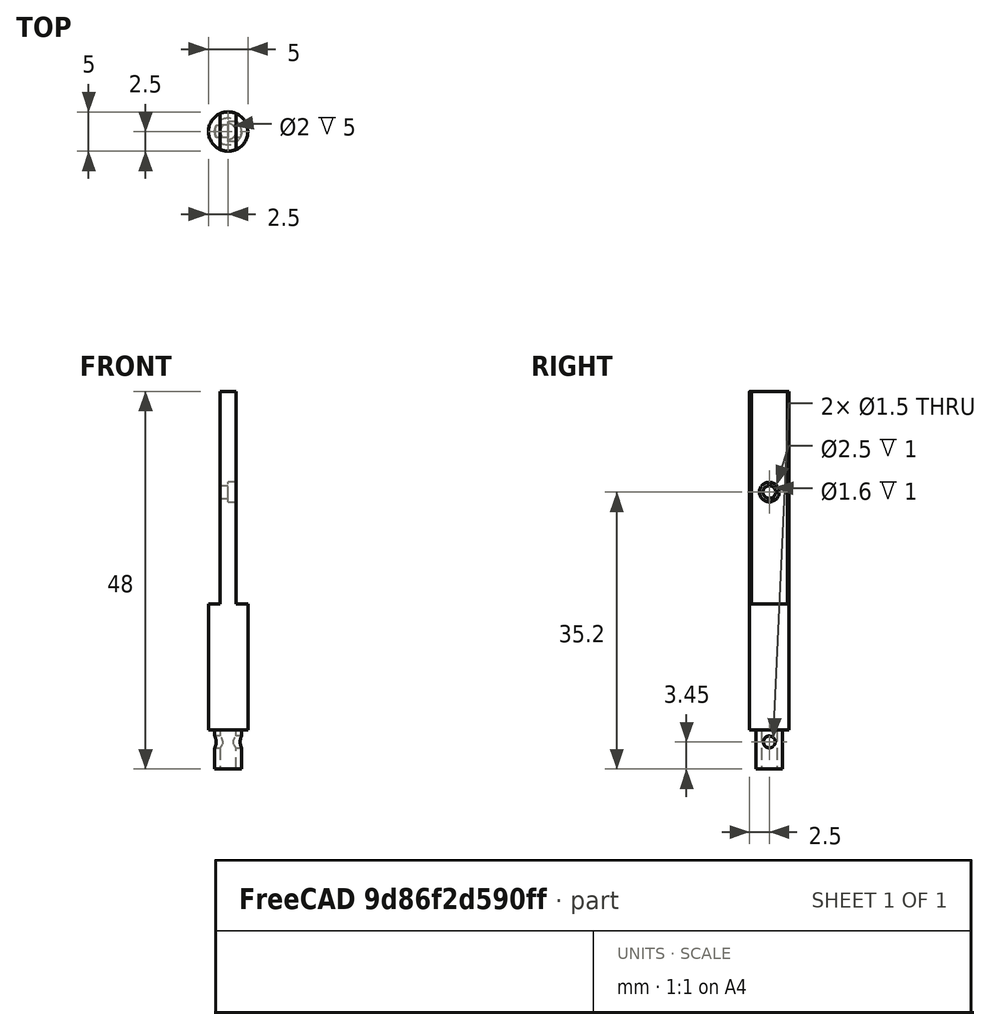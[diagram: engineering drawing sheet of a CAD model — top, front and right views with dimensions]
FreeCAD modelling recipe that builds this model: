
FCSTD DOCUMENT  (FreeCAD 0.20R29603 (Git))
Label: temholder
License: All rights reserved
LicenseURL: http://en.wikipedia.org/wiki/All_rights_reserved
objects: Part::Cylinder×7, Part::Cut×4, Part::MultiFuse×2, Part::Box×1, Part::MultiCommon×1, Part::Feature×1
note: 16 computed .brp shape members not serialized (recipe doc carries the construction recipe); baked Part::Feature solids carry a one-line shape summary decoded from their .brp

FEATURE [Part::Cylinder] Cylinder  label="Zylinder"
  Angle = 360
  AttacherType = Attacher::AttachEngine3D
  FirstAngle = 0
  Height = 21
  Radius = 1.7
  SecondAngle = 0
FEATURE [Part::Cylinder] Cylinder001  label="Zylinder001"
  Angle = 360
  AttacherType = Attacher::AttachEngine3D
  FirstAngle = 0
  Height = 16
  Placement = pos=(0,0,5) rot=(0,0,1;0rad)
  Radius = 2.5
  SecondAngle = 0
FEATURE [Part::Cylinder] Cylinder002  label="Zylinder002"
  Angle = 360
  AttacherType = Attacher::AttachEngine3D
  FirstAngle = 0
  Height = 6.5
  Placement = pos=(-3.25,0,3.45) rot=(0,1,0;1.5708rad)
  Radius = 0.75
  SecondAngle = 0
FEATURE [Part::MultiFuse] Fusion
  Shapes = -> [Cylinder,Cylinder001]
FEATURE [Part::Cut] Cut
  Base = -> Fusion
  Tool = -> Cylinder002
FEATURE [Part::Box] Box  label="Würfel"
  AttacherType = Attacher::AttachEngine3D
  Height = 27
  Length = 2
  Placement = pos=(-1,-5,21) rot=(0,0,1;0rad)
  Width = 10
FEATURE [Part::Cylinder] Cylinder003  label="BeamHole"
  Angle = 360
  AttacherType = Attacher::AttachEngine3D
  FirstAngle = 0
  Height = 2
  Placement = pos=(-1,0,35.2) rot=(0,1,0;1.5708rad)
  Radius = 0.8
  SecondAngle = 0
FEATURE [Part::Cylinder] Cylinder004  label="Zylinder004"
  Angle = 360
  AttacherType = Attacher::AttachEngine3D
  FirstAngle = 0
  Height = 27
  Placement = pos=(0,0,21) rot=(0,0,1;0rad)
  Radius = 2.5
  SecondAngle = 0
FEATURE [Part::MultiCommon] Common
  Shapes = -> [Cylinder004,Box]
FEATURE [Part::Cut] Cut001
  Base = -> Common
  Tool = -> Cylinder003
FEATURE [Part::Cylinder] Cylinder005  label="Zylinder005"
  Angle = 360
  AttacherType = Attacher::AttachEngine3D
  FirstAngle = 0
  Height = 5
  Radius = 1
  SecondAngle = 0
FEATURE [Part::Cut] Cut002
  Base = -> Cut
  Tool = -> Cylinder005
FEATURE [Part::Cylinder] Cylinder006  label="ProbeHole"
  Angle = 360
  AttacherType = Attacher::AttachEngine3D
  FirstAngle = 0
  Height = 10
  Placement = pos=(0,0,35.2) rot=(0,1,0;1.5708rad)
  Radius = 1.25
  SecondAngle = 0
FEATURE [Part::Cut] Cut003
  Base = -> Cut001
  Tool = -> Cylinder006
FEATURE [Part::MultiFuse] Fusion001
  Shapes = -> [Cut002,Cut003]
FEATURE [Part::Feature] Fusion001_solid  label="Fusion001 (Solid)"
  shape: bbox 5 x 5 x 48 mm, 20 faces (baked)
